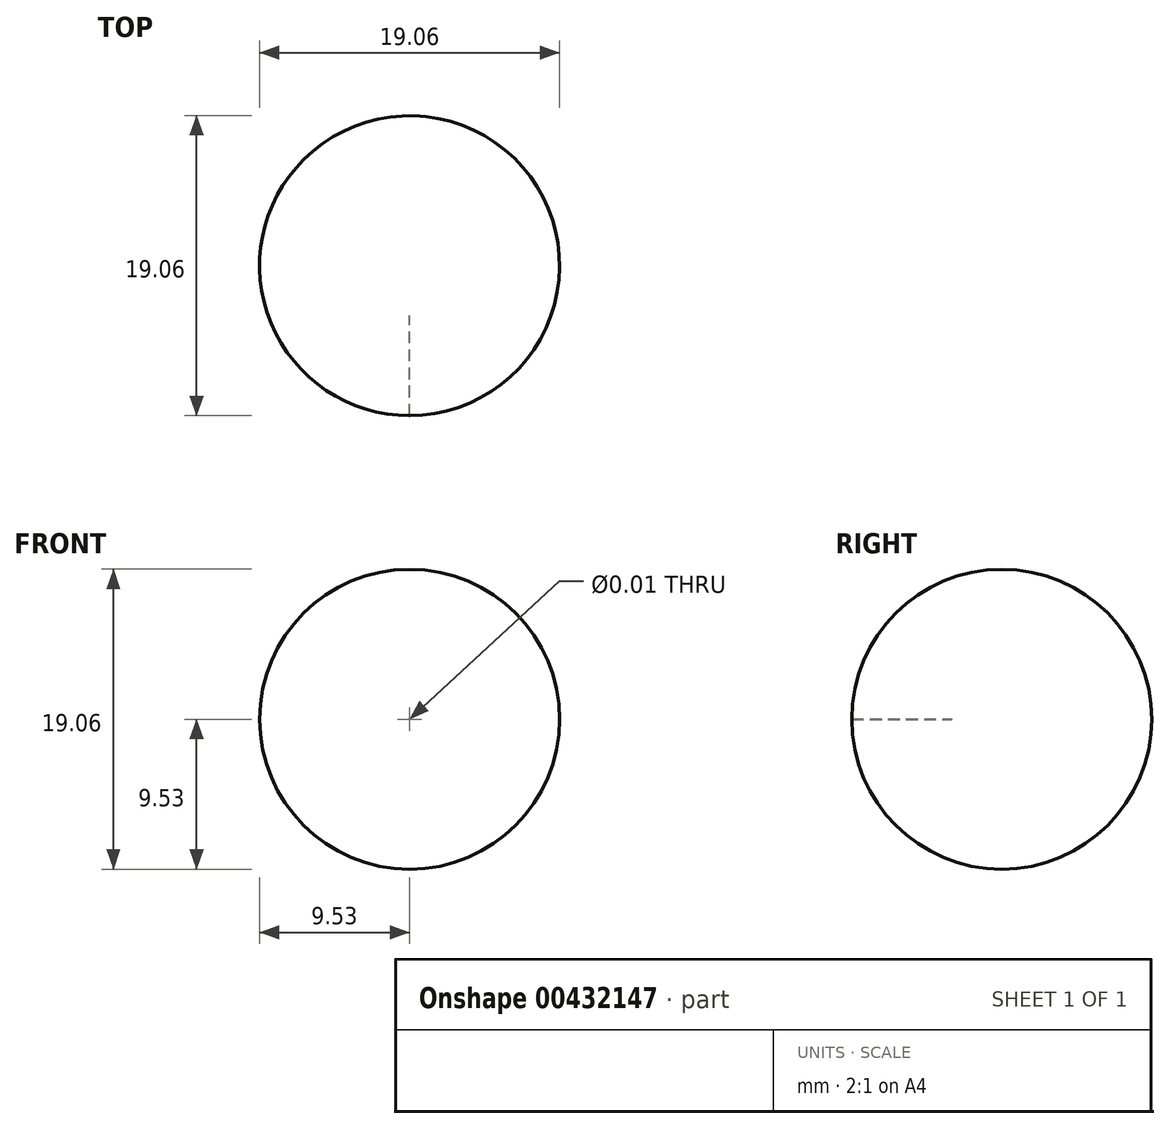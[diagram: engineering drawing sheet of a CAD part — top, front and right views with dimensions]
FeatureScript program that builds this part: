
annotation { "Feature Type Name" : "Feature", "Feature Type Description" : "" }
export const myFeature = defineFeature(function(context is Context, id is Id, definition is map)
    precondition{}
    {
        {
            var Q0;
            Q0=qCreatedBy(makeId("Front.planeOp"),FACE);
            var sketch = newSketch(context, id + "F0", { "sketchPlane" : qUnion([Q0])});
            skArc(sketch, "E0", {"start": v(0, -9.53) * mm, "mid": v(9.53, 0) * mm, "end": v(0, 9.53) * mm});
            skLineSegment(sketch, "E1", {"start": v(0, 9.53) * mm, "end": v(0, -9.53) * mm});
            skPoint(sketch, "E2.orphan", {"position": v(0, 22.36) * mm});
            skSolve(sketch);
        }
        {
            var Q0;
            Q0=makeQuery(id+"F0.imprint","IMPRINT",FACE,{"disambiguationData":[TD([[makeQuery(id+"F0.imprint","IMPRINT",EDGE,{"derivedFrom":sQuery(id+"F0.wireOp",EDGE,"E0")}),1.0]])]});
            var Q1;
            Q1=sQuery(id+"F0.wireOp",EDGE,"E1");
            revolve(context, id + "F1", {"entities" : qUnion([Q0]), "axis" : qUnion([Q1]), "revolveType" : RevolveType.FULL});
        }
        {
            var Q0;
            Q0=qCreatedBy(makeId("Front.planeOp"),FACE);
            cPlane(context, id + "F2", {"entities" : qUnion([Q0]), "cplaneType" : CPlaneType.OFFSET, "offset" : 9.52 * mm, "width" : 152.4 * mm, "height" : 152.4 * mm});
        }
        {
            var Q0;
            Q0=qCreatedBy(id+"F2.planeOp",FACE);
            var sketch = newSketch(context, id + "F3", { "sketchPlane" : qUnion([Q0])});
            skPoint(sketch, "E3", {"position": v(0, 0) * mm});
            skSolve(sketch);
        }
        {
            var Q0;
            Q0=sQuery(id+"F3.wireOp",VERTEX,"E3");
            var Q1;
            Q1=makeQuery(id+"F1.opRevolve","SWEPT_BODY",BODY,{"disambiguationData":[OSD([sQuery(id+"F0.wireOp",EDGE,"E0"),sQuery(id+"F0.wireOp",EDGE,"E1")])]});
            hole(context, id + "F4", {"style" : HoleStyle.SIMPLE, "endStyle" : HoleEndStyle.BLIND, "standardTappedOrClearance" : lookupTablePath({ "standard" : "ANSI", "size" : "3/8 (0.38)", "type" : "Drilled" }), "standardBlindInLast" : lookupTablePath({ "standard" : "ANSI", "size" : "3/8", "type" : "Drilled" }), "holeDiameter" : 3 / 203.2 * mm, "holeDepth" : 6.35 * mm, "isTappedThrough" : true, "tappedDepth" : 12.7 * mm, "tapClearance" : 3, "locations" : qUnion([Q0]), "scope" : qUnion([Q1]), "startStyle" : HoleStartStyle.SKETCH});
        }
    });
